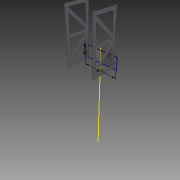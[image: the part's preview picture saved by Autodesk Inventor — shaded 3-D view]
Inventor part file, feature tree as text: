
AUTODESK INVENTOR PART (.ipt)
format: ipt  version: 2017 (Build 210142000, 142)  size: 187,392 bytes
history: native  units: mm
features: sketch x5, other x4, reference x4, hole x3, extrude x2, sheet_metal_op x1, plane x1
ambient origin geometry x8: Origin, YZ Plane, XZ Plane, XY Plane, X Axis, Y Axis, Z Axis, Center Point
bodies: Solid1 (feature_tree)
feature tree (20):
  sketch  "Sketch1"  dims[d0=180.0mm d2=3.0mm]
  sheet_metal_op  "Face1"
  hole  "Hole1"  [1 undecoded]
  plane  "Work Plane1"
  hole  "Hole3"  [1 undecoded]
  extrude  "Extrusion3"  Depth=60.0mm
  sketch  "Sketch10"  dims[d56=10.0mm d57=5.0mm d58=4.0mm d59=6.0mm d60=4.0mm d61=2.0mm d62=90.0deg d63=3.0mm d64=20.594885mm d65=3.0mm d66=140.0mm d67=120.0mm d68=260.0mm d69=0.0mm d70=15.0mm d71=15.0mm d72=15.0mm d73=15.0mm d74=15.0mm d75=15.0mm d77=15.0mm d78=300.0mm d79=0.0mm d80=8.0mm d81=8.0mm d82=8.0mm d83=8.0mm d84=4.0mm d85=6.0mm d86=4.0mm d87=2.0mm d88=90.0deg d89=3.0mm d90=20.594885mm]
  extrude  "Extrusion4"  Depth=3.0mm
  hole  "Hole4"  [1 undecoded]
  other  "Plate1"
  sketch  "Sketch2"  dims[d4=8.2mm]
  reference  "Reference3"
  reference  "Reference4"
  reference  "Reference5"
  reference  "Reference6"
  sketch  "Sketch8"  dims[d5=4.0mm d6=6.0mm d7=4.0mm d8=2.0mm d9=90.0deg d10=3.0mm d11=20.594885mm]
  sketch  "Sketch9"  dims[d31=86.0mm d34=60.0mm]
  parser-record x1  (decoder bookkeeping rows leaked as tree rows — omitted from the tree; the rows remain in map.json)
  other  "Balloon Assembly.iam"
  other  "LENS MOUNT:1"
note: 3 required parameter values undecoded (feature->parameter linkage not recoverable at this tier; creation-order binding heuristic only, values carry confidence <= 0.55)
note: 1 file-system path scrubbed to <path> (originals preserved in map.json)
